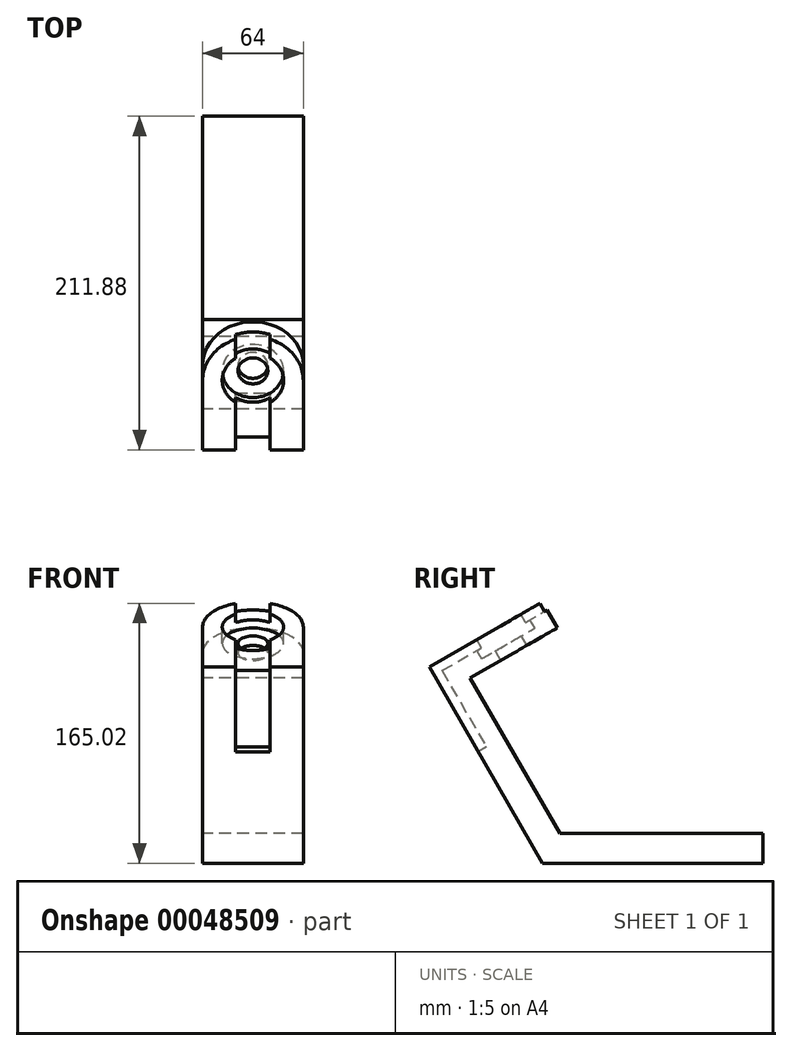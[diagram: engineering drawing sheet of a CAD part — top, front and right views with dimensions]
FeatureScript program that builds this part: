
annotation { "Feature Type Name" : "Feature", "Feature Type Description" : "" }
export const myFeature = defineFeature(function(context is Context, id is Id, definition is map)
    precondition{}
    {
        {
            var Q0;
            Q0=qCreatedBy(makeId("Right.planeOp"),FACE);
            var sketch = newSketch(context, id + "F0", { "sketchPlane" : qUnion([Q0])});
            skLineSegment(sketch, "E0", {"start": v(140, 0) * mm, "end": v(0, 0) * mm});
            skLineSegment(sketch, "E1", {"start": v(0, 0) * mm, "end": v(-71.88, 124.5) * mm});
            skLineSegment(sketch, "E2", {"start": v(-71.88, 124.5) * mm, "end": v(0, 166) * mm});
            skLineSegment(sketch, "E3.0", {"start": v(-45.93, 117.55) * mm, "end": v(9.5, 149.55) * mm});
            skLineSegment(sketch, "E3.1", {"start": v(10.97, 19) * mm, "end": v(-45.93, 117.55) * mm});
            skLineSegment(sketch, "E3.2", {"start": v(140, 19) * mm, "end": v(10.97, 19) * mm});
            skLineSegment(sketch, "E4", {"start": v(9.5, 149.55) * mm, "end": v(0, 166) * mm});
            skLineSegment(sketch, "E5", {"start": v(140, 0) * mm, "end": v(140, 19) * mm});
            skSolve(sketch);
        }
        {
            var Q0;
            Q0=makeQuery(id+"F0.imprint","IMPRINT",FACE,{"disambiguationData":[TD([[makeQuery(id+"F0.imprint","IMPRINT",EDGE,{"derivedFrom":sQuery(id+"F0.wireOp",EDGE,"E0")}),-1.0]])]});
            extrude(context, id + "F1", {"entities" : qUnion([Q0]), "endBound" : BoundingType.SYMMETRIC, "depth" : 64 * mm});
        }
        {
            var Q0;
            Q0=makeQuery(id+"F1.opExtrude","SWEPT_FACE",FACE,{"disambiguationData":[OSD([sQuery(id+"F0.wireOp",EDGE,"E2")])]});
            var sketch = newSketch(context, id + "F2", { "sketchPlane" : qUnion([Q0])});
            skPoint(sketch, "E6", {"position": v(0, 51) * mm});
            skPoint(sketch, "E6.positionSnap0", {"position": v(0, 83) * mm});
            skCircle(sketch, "E7", {"center": v(0, 51) * mm, "radius": 32 * mm});
            skCircle(sketch, "E8", {"center": v(0, 51) * mm, "radius": 19.5 * mm});
            skCircle(sketch, "E9", {"center": v(0, 51) * mm, "radius": 9.5 * mm});
            skSolve(sketch);
        }
        {
            var Q0;
            {var subQ0=sQuery(id+"F0.wireOp",EDGE,"E2");var subQ2=sQuery(id+"F2.wireOp",EDGE,"E7");var subQ4=makeQuery(id+"F1.opExtrude","CAP_EDGE",EDGE,{"disambiguationData":[OSD([subQ0])],"isStart":false});var subQ6=makeQuery(id+"F2.imprint","INTERSECT",VERTEX,{"derivedFrom":[subQ4,subQ2]});Q0=makeQuery(id+"F2.imprint","IMPRINT",FACE,{"disambiguationData":[TD([[makeQuery(id+"F2.imprint","IMPRINT",EDGE,{"disambiguationData":[TD([[subQ6,-1.0]])],"derivedFrom":subQ2}),-1.0]])]});}
            var Q1;
            {var subQ0=sQuery(id+"F0.wireOp",EDGE,"E2");var subQ2=sQuery(id+"F2.wireOp",EDGE,"E7");var subQ4=makeQuery(id+"F1.opExtrude","CAP_EDGE",EDGE,{"disambiguationData":[OSD([subQ0])],"isStart":true});var subQ6=makeQuery(id+"F2.imprint","INTERSECT",VERTEX,{"derivedFrom":[subQ4,subQ2]});Q1=makeQuery(id+"F2.imprint","IMPRINT",FACE,{"disambiguationData":[TD([[makeQuery(id+"F2.imprint","IMPRINT",EDGE,{"disambiguationData":[TD([[subQ6,1.0]])],"derivedFrom":subQ2}),-1.0]])]});}
            var Q2;
            Q2=makeQuery(id+"F2.imprint","IMPRINT",FACE,{"disambiguationData":[TD([[makeQuery(id+"F2.imprint","IMPRINT",EDGE,{"derivedFrom":sQuery(id+"F2.wireOp",EDGE,"E9")}),1.0]])]});
            extrude(context, id + "F3", {"entities" : qUnion([Q0, Q1, Q2]), "operationType" : NewBodyOperationType.REMOVE, "endBound" : BoundingType.UP_TO_NEXT, "oppositeDirection" : true, "depth" : 25 * mm});
        }
        {
            var Q0;
            Q0=makeQuery(id+"F2.imprint","IMPRINT",FACE,{"disambiguationData":[TD([[makeQuery(id+"F2.imprint","IMPRINT",EDGE,{"derivedFrom":sQuery(id+"F2.wireOp",EDGE,"E8")}),1.0]])]});
            extrude(context, id + "F4", {"entities" : qUnion([Q0]), "operationType" : NewBodyOperationType.REMOVE, "oppositeDirection" : true, "depth" : 12 * mm});
        }
        {
            var Q0;
            {var subQ0=sQuery(id+"F0.wireOp",EDGE,"E2");var subQ1=makeQuery(id+"F1.opExtrude","SWEPT_EDGE",EDGE,{"disambiguationData":[OSD([sQuery(id+"F0.wireOp",EDGE,"E1"),subQ0])]});Q0=makeQuery(id+"F2.imprint","IMPRINT",FACE,{"disambiguationData":[TD([[makeQuery(id+"F2.imprint","IMPRINT",EDGE,{"derivedFrom":subQ1}),-1.0]])]});}
            var sketch = newSketch(context, id + "F5", { "sketchPlane" : qUnion([Q0])});
            skLineSegment(sketch, "E10.bottom", {"start": v(11, 0) * mm, "end": v(-11, 0) * mm});
            skLineSegment(sketch, "E10.top", {"start": v(11, 83) * mm, "end": v(-11, 83) * mm});
            skLineSegment(sketch, "E10.left", {"start": v(11, 0) * mm, "end": v(11, 83) * mm});
            skLineSegment(sketch, "E10.right", {"start": v(-11, 0) * mm, "end": v(-11, 83) * mm});
            skSolve(sketch);
        }
        {
            var Q0;
            {var subQ8=sQuery(id+"F5.wireOp",EDGE,"E10.bottom");Q0=makeQuery(id+"F5.imprint","IMPRINT",FACE,{"disambiguationData":[TD([[makeQuery(id+"F5.imprint","IMPRINT",EDGE,{"derivedFrom":subQ8}),-1.0]])]});}
            var Q1;
            {var subQ7=sQuery(id+"F5.wireOp",EDGE,"E10.top");Q1=makeQuery(id+"F5.imprint","IMPRINT",FACE,{"disambiguationData":[TD([[makeQuery(id+"F5.imprint","IMPRINT",EDGE,{"derivedFrom":subQ7}),1.0]])]});}
            extrude(context, id + "F6", {"entities" : qUnion([Q0, Q1]), "operationType" : NewBodyOperationType.REMOVE, "oppositeDirection" : true, "depth" : 6 * mm});
        }
        {
            var Q0;
            Q0=makeQuery(id+"F1.opExtrude","SWEPT_FACE",FACE,{"disambiguationData":[OSD([sQuery(id+"F0.wireOp",EDGE,"E1")])]});
            var sketch = newSketch(context, id + "F7", { "sketchPlane" : qUnion([Q0])});
            skLineSegment(sketch, "E11.bottom", {"start": v(-11, 137.76) * mm, "end": v(11, 137.76) * mm});
            skLineSegment(sketch, "E11.top", {"start": v(-11, 81.76) * mm, "end": v(11, 81.76) * mm});
            skLineSegment(sketch, "E11.left", {"start": v(-11, 137.76) * mm, "end": v(-11, 81.76) * mm});
            skLineSegment(sketch, "E11.right", {"start": v(11, 137.76) * mm, "end": v(11, 81.76) * mm});
            skSolve(sketch);
        }
        {
            var Q0;
            Q0=makeQuery(id+"F7.imprint","IMPRINT",FACE,{"disambiguationData":[TD([[makeQuery(id+"F7.imprint","IMPRINT",EDGE,{"derivedFrom":sQuery(id+"F7.wireOp",EDGE,"E11.bottom")}),1.0]])]});
            extrude(context, id + "F8", {"entities" : qUnion([Q0]), "operationType" : NewBodyOperationType.REMOVE, "oppositeDirection" : true, "depth" : 6 * mm});
        }
    });
